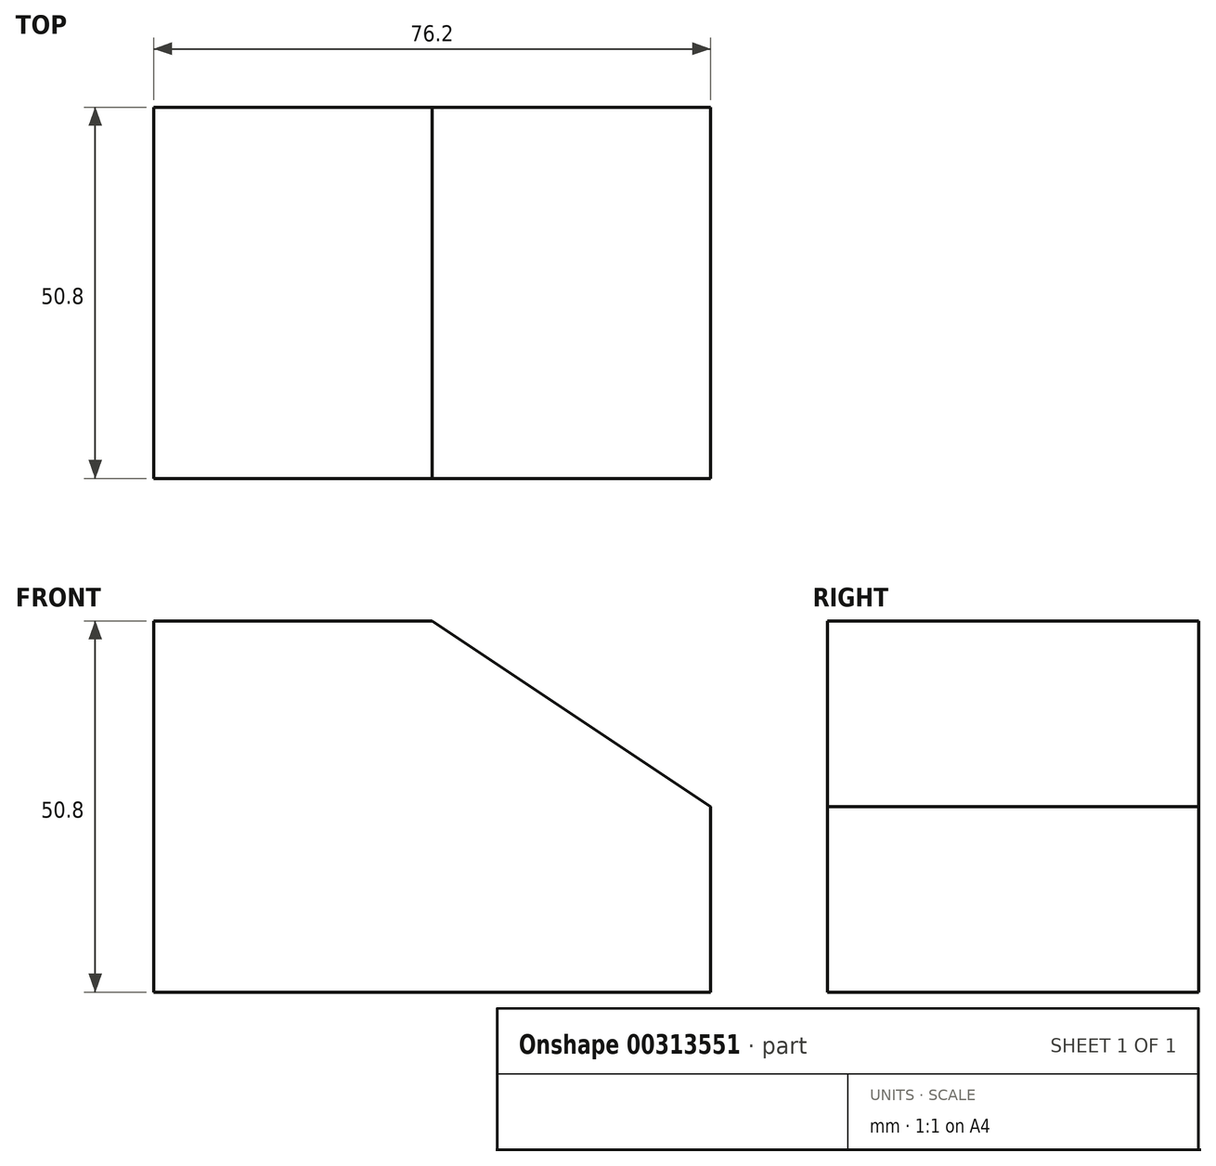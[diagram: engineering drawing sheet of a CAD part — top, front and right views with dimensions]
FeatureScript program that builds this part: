
annotation { "Feature Type Name" : "Feature", "Feature Type Description" : "" }
export const myFeature = defineFeature(function(context is Context, id is Id, definition is map)
    precondition{}
    {
        {
            var Q0;
            Q0=qCreatedBy(makeId("Front.planeOp"),FACE);
            var sketch = newSketch(context, id + "F0", { "sketchPlane" : qUnion([Q0])});
            skLineSegment(sketch, "E0", {"start": v(-41.54, -40.64) * mm, "end": v(34.66, -40.64) * mm});
            skLineSegment(sketch, "E1", {"start": v(34.66, -40.64) * mm, "end": v(34.66, -15.24) * mm});
            skLineSegment(sketch, "E2", {"start": v(-41.54, -40.64) * mm, "end": v(-41.54, 10.16) * mm});
            skLineSegment(sketch, "E3", {"start": v(-41.54, 10.16) * mm, "end": v(-3.44, 10.16) * mm});
            skLineSegment(sketch, "E4", {"start": v(-3.44, 10.16) * mm, "end": v(34.66, -15.24) * mm});
            skSolve(sketch);
        }
        {
            var Q0;
            Q0=makeQuery(id+"F0.imprint","IMPRINT",FACE,{"disambiguationData":[TD([[makeQuery(id+"F0.imprint","IMPRINT",EDGE,{"derivedFrom":sQuery(id+"F0.wireOp",EDGE,"E0")}),1.0]])]});
            extrude(context, id + "F1", {"entities" : qUnion([Q0]), "depth" : 50.8 * mm});
        }
    });
